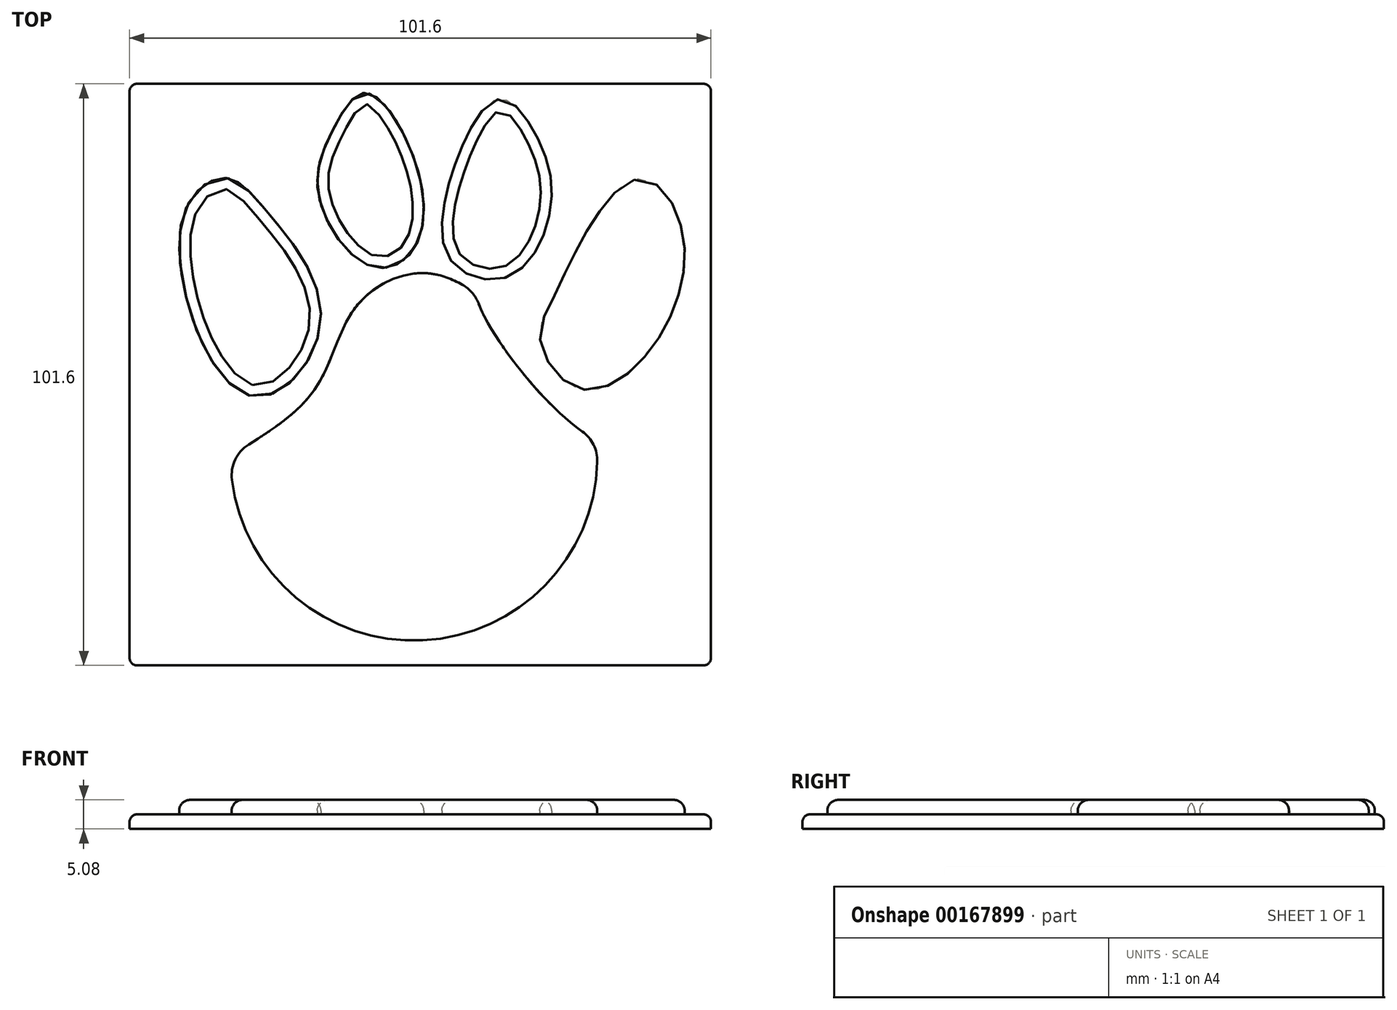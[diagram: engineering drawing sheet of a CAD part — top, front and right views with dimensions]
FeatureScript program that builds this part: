
annotation { "Feature Type Name" : "Feature", "Feature Type Description" : "" }
export const myFeature = defineFeature(function(context is Context, id is Id, definition is map)
    precondition{}
    {
        {
            var Q0;
            Q0=qCreatedBy(makeId("Top.planeOp"),FACE);
            var sketch = newSketch(context, id + "F0", { "sketchPlane" : qUnion([Q0])});
            skLineSegment(sketch, "E0.bottom", {"start": v(50.8, 50.8) * mm, "end": v(-50.8, 50.8) * mm});
            skLineSegment(sketch, "E0.top", {"start": v(50.8, -50.8) * mm, "end": v(-50.8, -50.8) * mm});
            skLineSegment(sketch, "E0.left", {"start": v(50.8, 50.8) * mm, "end": v(50.8, -50.8) * mm});
            skLineSegment(sketch, "E0.right", {"start": v(-50.8, 50.8) * mm, "end": v(-50.8, -50.8) * mm});
            skSolve(sketch);
        }
        {
            var Q0;
            Q0=makeQuery(id+"F0.imprint","IMPRINT",FACE,{"disambiguationData":[TD([[makeQuery(id+"F0.imprint","IMPRINT",EDGE,{"derivedFrom":sQuery(id+"F0.wireOp",EDGE,"E0.bottom")}),1.0]])]});
            extrude(context, id + "F1", {"entities" : qUnion([Q0]), "depth" : 2.54 * mm});
        }
        {
            var Q0;
            Q0=makeQuery(id+"F1.opExtrude","CAP_FACE",FACE,{"disambiguationData":[OSD([sQuery(id+"F0.wireOp",EDGE,"E0.bottom"),sQuery(id+"F0.wireOp",EDGE,"E0.top"),sQuery(id+"F0.wireOp",EDGE,"E0.left"),sQuery(id+"F0.wireOp",EDGE,"E0.right")])],"isStart":false});
            var sketch = newSketch(context, id + "F2", { "sketchPlane" : qUnion([Q0])});
            skPoint(sketch, "E1.middle", {"position": v(-1.1, 2.32) * mm});
            skArc(sketch, "E2", {"start": v(-32.91, -18.37) * mm, "mid": v(0.46, -46.42) * mm, "end": v(30.94, -15.26) * mm});
            skFitSpline(sketch, "E3", {"points": [v(9.59, 14.3) * mm, v(21.95, -4.32) * mm, v(30.83, -11.61) * mm], "startDerivative": vector(6.75, -28.22) * mm, "endDerivative": vector(20.93, -12.99) * mm});
            skArc(sketch, "E4.trimOffspring", {"start": v(-1.07, 17.65) * mm, "mid": v(-1.09, 17.65) * mm, "end": v(-1.1, 17.65) * mm});
            skFitSpline(sketch, "E5", {"points": [v(-33.16, -14.19) * mm, v(-18.4, -2.5) * mm, v(-11.4, 11.65) * mm, v(-1.07, 17.65) * mm, v(9.59, 14.3) * mm], "startDerivative": vector(61.53, 38.74) * mm, "endDerivative": vector(53, -36.24) * mm});
            skArc(sketch, "E6.filletArc", {"start": v(10.18, 12.44) * mm, "mid": v(9.06, 14.3) * mm, "end": v(7.37, 15.69) * mm});
            skArc(sketch, "E7.filletArc", {"start": v(-29.99, -12.2) * mm, "mid": v(-32.35, -14.86) * mm, "end": v(-32.91, -18.37) * mm});
            skArc(sketch, "E8.filletArc", {"start": v(30.94, -15.26) * mm, "mid": v(30.28, -12.26) * mm, "end": v(28.29, -9.93) * mm});
            skFitSpline(sketch, "E9", {"points": [v(-29.85, -3.68) * mm, v(-17.42, 9.03) * mm, v(-26.88, 28.6) * mm, v(-34.2, 34.36) * mm, v(-41.89, 25.81) * mm, v(-29.85, -3.68) * mm]});
            skFitSpline(sketch, "E10", {"points": [v(-9.26, 19.18) * mm, v(-1.93, 20.93) * mm, v(0, 34.01) * mm, v(-9.26, 49.2) * mm, v(-15.01, 43.26) * mm, v(-17.8, 31.57) * mm, v(-9.26, 19.18) * mm]});
            skFitSpline(sketch, "E11", {"points": [v(5.4, 19.88) * mm, v(5.75, 35.76) * mm, v(13.78, 48.15) * mm, v(20.06, 42.21) * mm, v(22.85, 29.65) * mm, v(15.7, 17.26) * mm, v(5.4, 19.88) * mm]});
            skFitSpline(sketch, "E12", {"points": [v(20.93, 6.1) * mm, v(27.74, -2.46) * mm, v(39.95, 4) * mm, v(45.88, 24.6) * mm, v(38.03, 34.19) * mm, v(26.7, 20.58) * mm, v(22.85, 12.55) * mm, v(20.93, 6.1) * mm]});
            skSolve(sketch);
        }
        {
            var Q0;
            Q0=makeQuery(id+"F2.imprint","IMPRINT",FACE,{"disambiguationData":[TD([[makeQuery(id+"F2.imprint","IMPRINT",EDGE,{"derivedFrom":sQuery(id+"F2.wireOp",EDGE,"E2")}),1.0]])]});
            var Q1;
            Q1=makeQuery(id+"F2.imprint","IMPRINT",FACE,{"disambiguationData":[TD([[makeQuery(id+"F2.imprint","IMPRINT",EDGE,{"derivedFrom":sQuery(id+"F2.wireOp",EDGE,"E10")}),1.0]])]});
            var Q2;
            Q2=makeQuery(id+"F2.imprint","IMPRINT",FACE,{"disambiguationData":[TD([[makeQuery(id+"F2.imprint","IMPRINT",EDGE,{"derivedFrom":sQuery(id+"F2.wireOp",EDGE,"E11")}),-1.0]])]});
            var Q3;
            Q3=makeQuery(id+"F2.imprint","IMPRINT",FACE,{"disambiguationData":[TD([[makeQuery(id+"F2.imprint","IMPRINT",EDGE,{"derivedFrom":sQuery(id+"F2.wireOp",EDGE,"E12")}),1.0]])]});
            var Q4;
            Q4=makeQuery(id+"F2.imprint","IMPRINT",FACE,{"disambiguationData":[TD([[makeQuery(id+"F2.imprint","IMPRINT",EDGE,{"derivedFrom":sQuery(id+"F2.wireOp",EDGE,"E9")}),1.0]])]});
            extrude(context, id + "F3", {"entities" : qUnion([Q0, Q1, Q2, Q3, Q4]), "operationType" : NewBodyOperationType.ADD, "depth" : 2.54 * mm});
        }
        {
            var Q0;
            Q0=makeQuery(id+"F3.opExtrude","CAP_EDGE",EDGE,{"disambiguationData":[OSD([sQuery(id+"F2.wireOp",EDGE,"E9")])],"isStart":false});
            fillet(context, id + "F4", {"entities" : qUnion([Q0]), "radius" : 1.9 * mm, "tangentPropagation" : true, "allowEdgeOverflow" : false});
        }
        {
            var Q0;
            Q0=makeQuery(id+"F3.opExtrude","CAP_EDGE",EDGE,{"disambiguationData":[OSD([sQuery(id+"F2.wireOp",EDGE,"E10")])],"isStart":false});
            fillet(context, id + "F5", {"entities" : qUnion([Q0]), "radius" : 1.9 * mm, "tangentPropagation" : true, "allowEdgeOverflow" : false});
        }
        {
            var Q0;
            Q0=makeQuery(id+"F3.opExtrude","CAP_EDGE",EDGE,{"disambiguationData":[OSD([sQuery(id+"F2.wireOp",EDGE,"E11")])],"isStart":false});
            fillet(context, id + "F6", {"entities" : qUnion([Q0]), "radius" : 1.9 * mm, "tangentPropagation" : true, "allowEdgeOverflow" : false});
        }
        {
            var Q0;
            Q0=makeQuery(id+"F3.opExtrude","CAP_EDGE",EDGE,{"disambiguationData":[OSD([sQuery(id+"F2.wireOp",EDGE,"E12")])],"isStart":false});
            fillet(context, id + "F7", {"entities" : qUnion([Q0]), "radius" : 1.9 * mm, "tangentPropagation" : true, "allowEdgeOverflow" : false});
        }
        {
            var Q0;
            Q0=makeQuery(id+"F3.opExtrude","CAP_EDGE",EDGE,{"disambiguationData":[OSD([sQuery(id+"F2.wireOp",EDGE,"E5")])],"isStart":false});
            fillet(context, id + "F8", {"entities" : qUnion([Q0]), "radius" : 1.9 * mm, "tangentPropagation" : true, "allowEdgeOverflow" : false});
        }
        {
            var Q0;
            Q0=makeQuery(id+"F1.opExtrude","CAP_EDGE",EDGE,{"disambiguationData":[OSD([sQuery(id+"F0.wireOp",EDGE,"E0.right")])],"isStart":false});
            fillet(context, id + "F9", {"entities" : qUnion([Q0]), "radius" : 1.27 * mm, "tangentPropagation" : true, "allowEdgeOverflow" : false});
        }
        {
            var Q0;
            Q0=makeQuery(id+"F1.opExtrude","CAP_EDGE",EDGE,{"disambiguationData":[OSD([sQuery(id+"F0.wireOp",EDGE,"E0.top")])],"isStart":false});
            fillet(context, id + "F10", {"entities" : qUnion([Q0]), "radius" : 1.27 * mm, "tangentPropagation" : true, "allowEdgeOverflow" : false});
        }
        {
            var Q0;
            Q0=makeQuery(id+"F1.opExtrude","CAP_EDGE",EDGE,{"disambiguationData":[OSD([sQuery(id+"F0.wireOp",EDGE,"E0.left")])],"isStart":false});
            fillet(context, id + "F11", {"entities" : qUnion([Q0]), "radius" : 1.27 * mm, "tangentPropagation" : true, "allowEdgeOverflow" : false});
        }
        {
            var Q0;
            Q0=makeQuery(id+"F1.opExtrude","CAP_EDGE",EDGE,{"disambiguationData":[OSD([sQuery(id+"F0.wireOp",EDGE,"E0.bottom")])],"isStart":false});
            fillet(context, id + "F12", {"entities" : qUnion([Q0]), "radius" : 1.27 * mm, "tangentPropagation" : true, "allowEdgeOverflow" : false});
        }
    });
